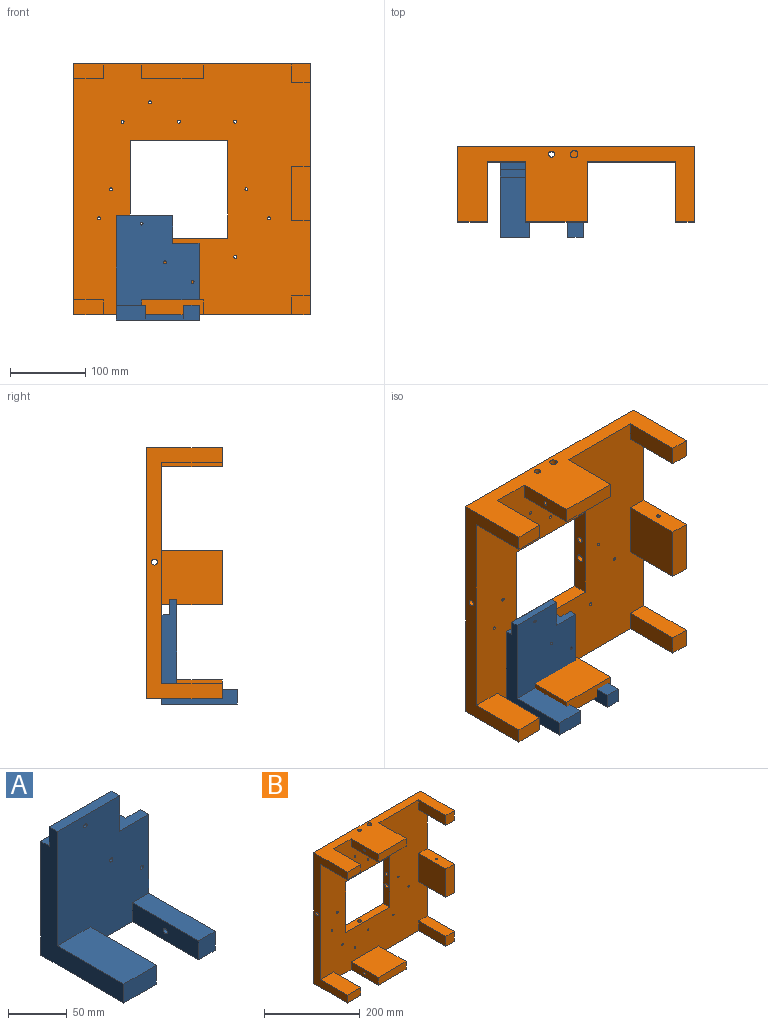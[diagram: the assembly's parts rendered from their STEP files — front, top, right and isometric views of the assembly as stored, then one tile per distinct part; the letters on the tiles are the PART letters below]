
ASSEMBLY  parts=2 mates=1
PART A: 22 faces, bbox 110.3x100x139 mm
  f0: plane 75x10mm, normal (0,0,1), area 750mm2, adj f2,f15,f16,f20
  f1: plane 75x10mm, normal (0,0,1), area 750mm2, adj f2,f15,f16,f21
  f2: plane 75x20mm, normal (0,1,0), area 1487.4mm2, adj f0,f1,f15,f16,f19
  f3: cylinder r=2.5mm len=20mm, axis (1,0,0), area 314.2mm2, adj f9,f11
  f4: plane 20x19.75mm, normal (0,-1,0), area 395mm2, adj f9,f10,f11,f12
  f5: plane 102x18mm, normal (0,1,0), area 1823.4mm2, adj f7,f8,f9,f12,f18
  f6: plane 39.49x19.75mm, normal (0,-1,0), area 780mm2, adj f12,f13,f14,f15
  f7: plane 102x10mm, normal (1,0,0), area 1020mm2, adj f5,f8,f12,f21
  f8: plane 35.25x20mm, normal (0,0,1), area 525.1mm2, adj f5,f7,f9,f16,f20,f21
  f9: plane 102x90mm, normal (1,0,0), area 2580.4mm2, adj f3,f4,f5,f8,f10,f12,f20
  f10: plane 80x20mm, normal (0,0,1), area 1600mm2, adj f4,f9,f11,f20
  f11: plane 80x19.75mm, normal (-1,0,0), area 1560.4mm2, adj f3,f4,f10,f12,f20
  f12: plane 110.25x100mm, normal (0,0,-1), area 6784.4mm2, adj f4,f5,f6,f7,f9,f11,f13,f15
  f13: plane 80x19.75mm, normal (1,0,0), area 1580mm2, adj f6,f12,f14,f20
  f14: plane 80x39.49mm, normal (0,0,1), area 3159.4mm2, adj f6,f13,f15,f20
  f15: plane 139x100mm, normal (-1,0,0), area 4160mm2, adj f0,f1,f2,f6,f12,f14,f20,f21
  f16: plane 37x20mm, normal (1,0,0), area 540mm2, adj f0,f1,f2,f8,f20,f21
  f17: cylinder r=2mm len=20mm, axis (0,1,0), area 251.3mm2, adj f20,f21
  f18: cylinder r=2mm len=10mm, axis (0,1,0), area 125.7mm2, adj f5,f20
  f19: cylinder r=2mm len=10mm, axis (0,1,0), area 125.7mm2, adj f2,f20
  f20: plane 139x110.25mm, normal (0,-1,0), area 12808.1mm2, adj f0,f8,f9,f10,f11,f12,f13,f14
  f21: plane 119x92.25mm, normal (0,1,0), area 10672.2mm2, adj f1,f7,f8,f12,f15,f16,f17
PART B: 55 faces, bbox 315x100x334 mm
  f0: plane 315x100mm, normal (0,0,1), area 17910.3mm2, adj f6,f7,f8,f9,f17,f18,f31,f32
  f1: plane 315x100mm, normal (0,0,-1), area 17988.9mm2, adj f6,f7,f8,f9,f16,f19,f28,f34
  f2: plane 82.25x80mm, normal (0,0,1), area 6579.8mm2, adj f9,f19,f34,f43
  f3: plane 82.25x80mm, normal (0,0,-1), area 6579.8mm2, adj f9,f18,f35,f44
  f4: plane 80x39.49mm, normal (0,0,1), area 3159.4mm2, adj f6,f9,f36,f41
  f5: plane 80x39.49mm, normal (0,0,-1), area 3159.4mm2, adj f6,f9,f37,f42
  f6: plane 334x100mm, normal (-1,0,0), area 9789.7mm2, adj f0,f1,f4,f5,f8,f9,f30,f36
  f7: plane 334x100mm, normal (1,0,0), area 16333.5mm2, adj f0,f1,f8,f9,f10,f29,f33,f38
  f8: plane 334x315mm, normal (0,1,0), area 88159.2mm2, adj f0,f1,f6,f7,f11,f12,f13,f14
  f9: plane 334x315mm, normal (0,-1,0), area 80293.5mm2, adj f0,f1,f2,f3,f4,f5,f6,f7
  f10: plane 80x25mm, normal (0,0,-1), area 1980.4mm2, adj f7,f9,f15,f40,f54
  f11: plane 130x20mm, normal (0,0,-1), area 2471.2mm2, adj f8,f9,f12,f14,f31,f32
  f12: plane 130x20mm, normal (1,0,0), area 2549.7mm2, adj f8,f9,f11,f13,f30
  f13: plane 130x20mm, normal (0,0,1), area 2549.7mm2, adj f8,f9,f12,f14,f28
  f14: plane 130x20mm, normal (-1,0,0), area 2471.2mm2, adj f8,f9,f11,f13,f29,f33
  f15: plane 80x72.28mm, normal (-1,0,0), area 5782.3mm2, adj f9,f10,f40,f47
  f16: plane 80x25mm, normal (-1,0,0), area 2000mm2, adj f1,f9,f39,f46
  f17: plane 80x25mm, normal (-1,0,0), area 2000mm2, adj f0,f9,f38,f45
  f18: plane 80x19.75mm, normal (1,0,0), area 1560.4mm2, adj f0,f3,f9,f35,f52
  f19: plane 80x19.75mm, normal (1,0,0), area 1560.4mm2, adj f1,f2,f9,f34,f53
  f20: cylinder r=2mm len=20mm, axis (0,1,0), area 251.3mm2, adj f8,f9
  f21: cylinder r=2mm len=20mm, axis (0,1,0), area 251.3mm2, adj f8,f9
  f22: cylinder r=2mm len=20mm, axis (0,1,0), area 251.3mm2, adj f8,f9
  f23: cylinder r=2mm len=20mm, axis (0,1,0), area 251.3mm2, adj f8,f9
  f24: cylinder r=2mm len=20mm, axis (0,1,0), area 251.3mm2, adj f8,f9
  f25: cylinder r=2mm len=20mm, axis (0,1,0), area 251.3mm2, adj f8,f9
  f26: cylinder r=2mm len=20mm, axis (0,1,0), area 251.3mm2, adj f8,f9
  f27: cylinder r=2mm len=20mm, axis (0,1,0), area 251.3mm2, adj f8,f9
  f28: cylinder r=4mm len=102mm, axis (0,0,1), area 2563.5mm2, adj f1,f13
  f29: cylinder r=4mm len=110mm, axis (1,0,0), area 2764.6mm2, adj f7,f14
  f30: cylinder r=4mm len=75mm, axis (1,0,0), area 1885mm2, adj f6,f12
  f31: cylinder r=4mm len=102mm, axis (0,0,-1), area 2563.5mm2, adj f0,f11
  f32: cylinder r=5mm len=102mm, axis (0,0,-1), area 3204.4mm2, adj f0,f11
  f33: cylinder r=5mm len=110mm, axis (-1,0,0), area 3455.8mm2, adj f7,f14
  f34: plane 82.25x19.75mm, normal (0,-1,0), area 1624.4mm2, adj f1,f2,f19,f43
  f35: plane 82.25x19.75mm, normal (0,-1,0), area 1624.4mm2, adj f0,f3,f18,f44
  f36: plane 39.49x19.75mm, normal (0,-1,0), area 780mm2, adj f1,f4,f6,f41
  f37: plane 39.49x19.75mm, normal (0,-1,0), area 780mm2, adj f0,f5,f6,f42
  f38: plane 25x25mm, normal (0,-1,0), area 625mm2, adj f0,f7,f17,f45
  f39: plane 25x25mm, normal (0,-1,0), area 625mm2, adj f1,f7,f16,f46
  f40: plane 72.28x25mm, normal (0,-1,0), area 1807mm2, adj f7,f10,f15,f47
  f41: plane 80x19.75mm, normal (1,0,0), area 1580mm2, adj f1,f4,f9,f36
  f42: plane 80x19.75mm, normal (1,0,0), area 1580mm2, adj f0,f5,f9,f37
  f43: plane 80x19.75mm, normal (-1,0,0), area 1560.4mm2, adj f1,f2,f9,f34,f53
  f44: plane 80x19.75mm, normal (-1,0,0), area 1560.4mm2, adj f0,f3,f9,f35,f52
  f45: plane 80x25mm, normal (0,0,-1), area 2000mm2, adj f7,f9,f17,f38
  f46: plane 80x25mm, normal (0,0,1), area 2000mm2, adj f7,f9,f16,f39
  f47: plane 80x25mm, normal (0,0,1), area 1980.4mm2, adj f7,f9,f15,f40,f54
  f48: cylinder r=2mm len=20mm, axis (0,1,0), area 251.3mm2, adj f8,f9
  f49: cylinder r=2mm len=20mm, axis (0,1,0), area 251.3mm2, adj f8,f9
  f50: cylinder r=2mm len=20mm, axis (0,1,0), area 251.3mm2, adj f8,f9
  f51: cylinder r=2mm len=20mm, axis (0,1,0), area 251.3mm2, adj f8,f9
  f52: cylinder r=2.5mm len=82.25mm, axis (1,0,0), area 1291.9mm2, adj f18,f44
  f53: cylinder r=2.5mm len=82.25mm, axis (1,0,0), area 1291.9mm2, adj f19,f43
  f54: cylinder r=2.5mm len=72.28mm, axis (0,0,1), area 1135.4mm2, adj f10,f47
PLACE A t=(68.63,-136.67,119.39)mm
PLACE B t=(12.05,-116.67,126.47)mm
MATE planar A.f21 <-> B.f48  axis (0,1,0) through (79.95,-24.67,-129.45)mm
